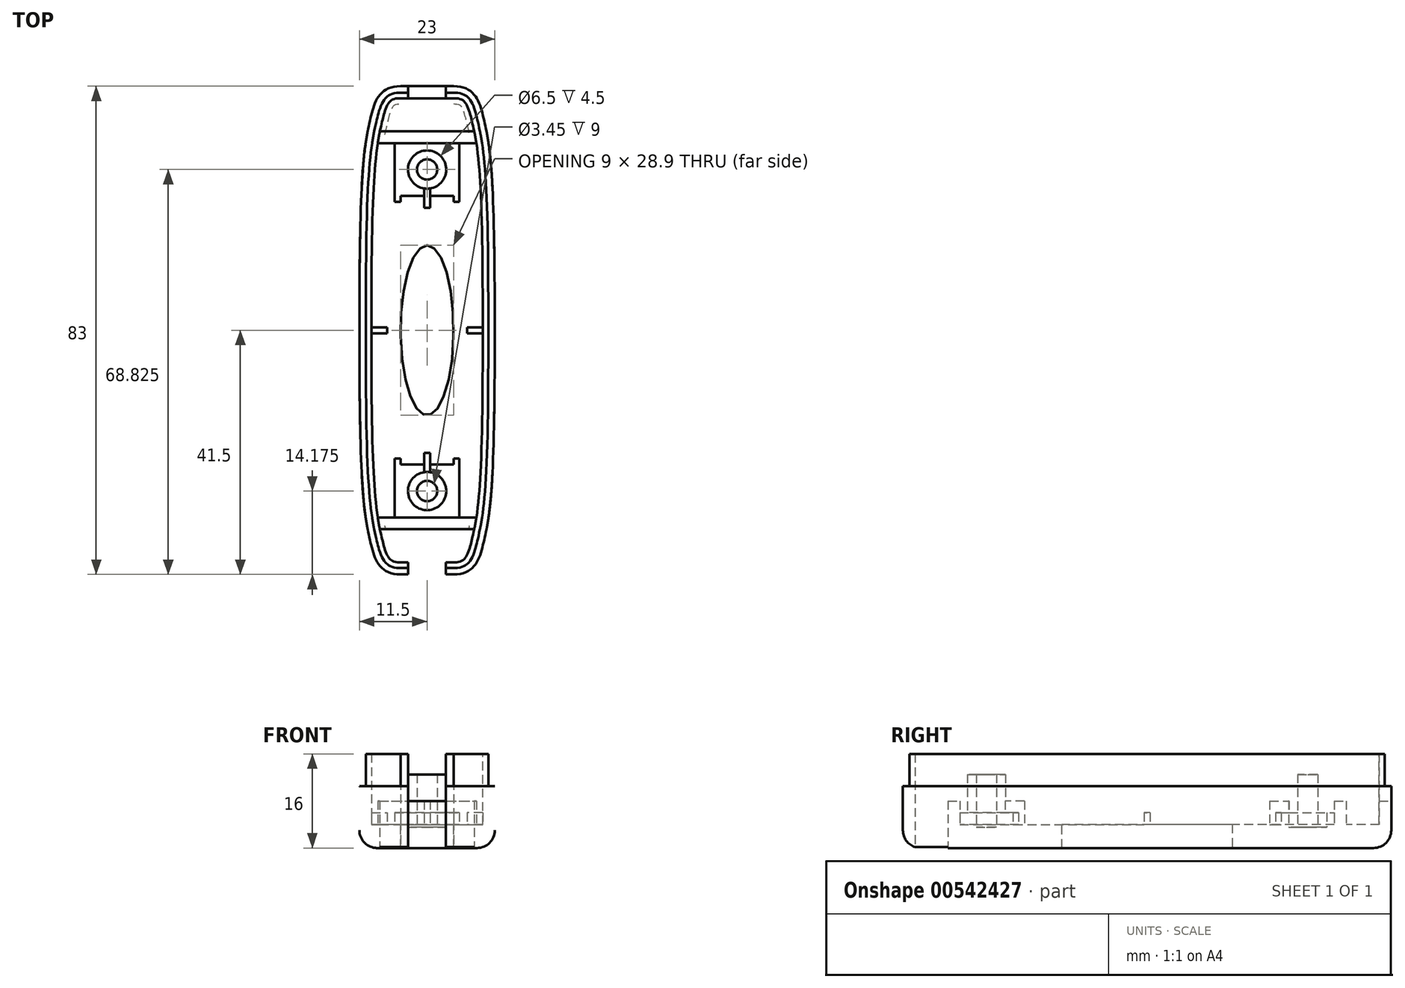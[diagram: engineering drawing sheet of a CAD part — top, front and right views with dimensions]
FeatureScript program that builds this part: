
annotation { "Feature Type Name" : "Feature", "Feature Type Description" : "" }
export const myFeature = defineFeature(function(context is Context, id is Id, definition is map)
    precondition{}
    {
        {
            var Q0;
            Q0=qCreatedBy(makeId("Top.planeOp"),FACE);
            var sketch = newSketch(context, id + "F0", { "sketchPlane" : qUnion([Q0])});
            skLineSegment(sketch, "E0.bottom", {"start": v(4.5, 14.45) * mm, "end": v(-4.5, 14.45) * mm, "construction": true});
            skLineSegment(sketch, "E0.top", {"start": v(4.5, -14.45) * mm, "end": v(-4.5, -14.45) * mm, "construction": true});
            skLineSegment(sketch, "E0.left", {"start": v(4.5, 14.45) * mm, "end": v(4.5, -14.45) * mm, "construction": true});
            skLineSegment(sketch, "E0.right", {"start": v(-4.5, 14.45) * mm, "end": v(-4.5, -14.45) * mm, "construction": true});
            skPoint(sketch, "E0.middle", {"position": v(0, 0) * mm});
            skPoint(sketch, "E1", {"position": v(0, 14.45) * mm});
            skPoint(sketch, "E2", {"position": v(4.5, 0) * mm});
            skEllipse(sketch, "E3", {"center": v(0, 0) * mm, "majorRadius": 14.45 * mm, "minorRadius": 4.5 * mm, "majorAxis": v(0, 1)});
            skLineSegment(sketch, "E4.bottom", {"start": v(11.5, 41.5) * mm, "end": v(-11.5, 41.5) * mm, "construction": true});
            skLineSegment(sketch, "E4.top", {"start": v(11.5, -41.5) * mm, "end": v(-11.5, -41.5) * mm, "construction": true});
            skLineSegment(sketch, "E4.left", {"start": v(11.5, 41.5) * mm, "end": v(11.5, -41.5) * mm, "construction": true});
            skLineSegment(sketch, "E4.right", {"start": v(-11.5, 41.5) * mm, "end": v(-11.5, -41.5) * mm, "construction": true});
            skLineSegment(sketch, "E5", {"start": v(11.5, 0) * mm, "end": v(-11.5, 0) * mm, "construction": true});
            skLineSegment(sketch, "E6.bottom", {"start": v(-11.5, 0.5) * mm, "end": v(-6.8, 0.5) * mm});
            skLineSegment(sketch, "E6.top", {"start": v(-11.5, -0.5) * mm, "end": v(-6.8, -0.5) * mm});
            skLineSegment(sketch, "E6.left", {"start": v(-11.5, 0.5) * mm, "end": v(-11.5, -0.5) * mm});
            skLineSegment(sketch, "E6.right", {"start": v(-6.8, 0.5) * mm, "end": v(-6.8, -0.5) * mm});
            skLineSegment(sketch, "E7.MirrorCS", {"start": v(6.8, 0.5) * mm, "end": v(6.8, -0.5) * mm});
            skLineSegment(sketch, "E8.MirrorCS", {"start": v(11.5, 0.5) * mm, "end": v(11.5, -0.5) * mm});
            skLineSegment(sketch, "E9.MirrorCS", {"start": v(11.5, -0.5) * mm, "end": v(6.8, -0.5) * mm});
            skLineSegment(sketch, "E10.MirrorCS", {"start": v(11.5, 0.5) * mm, "end": v(6.8, 0.5) * mm});
            skLineSegment(sketch, "E11.bottom", {"start": v(-9.5, 41.5) * mm, "end": v(9.5, 41.5) * mm, "construction": true});
            skLineSegment(sketch, "E11.top", {"start": v(-9.5, -41.5) * mm, "end": v(9.5, -41.5) * mm, "construction": true});
            skLineSegment(sketch, "E11.left", {"start": v(-9.5, 41.5) * mm, "end": v(-9.5, -41.5) * mm, "construction": true});
            skLineSegment(sketch, "E11.right", {"start": v(9.5, 41.5) * mm, "end": v(9.5, -41.5) * mm, "construction": true});
            skLineSegment(sketch, "E12", {"start": v(-9.5, -36.5) * mm, "end": v(9.5, -36.5) * mm, "construction": true});
            skLineSegment(sketch, "E13.MirrorCS", {"start": v(-9.5, 36.5) * mm, "end": v(9.5, 36.5) * mm, "construction": true});
            skLineSegment(sketch, "E14.bottom", {"start": v(-4.5, 41.5) * mm, "end": v(4.5, 41.5) * mm, "construction": true});
            skLineSegment(sketch, "E14.top", {"start": v(-4.5, -41.5) * mm, "end": v(4.5, -41.5) * mm, "construction": true});
            skLineSegment(sketch, "E14.left", {"start": v(-4.5, 41.5) * mm, "end": v(-4.5, -41.5) * mm, "construction": true});
            skLineSegment(sketch, "E14.right", {"start": v(4.5, 41.5) * mm, "end": v(4.5, -41.5) * mm, "construction": true});
            skLineSegment(sketch, "E15", {"start": v(-4.5, -41.5) * mm, "end": v(4.5, -41.5) * mm});
            skFitSpline(sketch, "E16", {"points": [v(4.5, -41.5) * mm, v(9.5, -36.5) * mm, v(11.5, 0) * mm], "startDerivative": vector(35.32, 0) * mm, "endDerivative": vector(0, 110.7) * mm});
            skFitSpline(sketch, "E17.MirrorCS", {"points": [v(-4.5, -41.5) * mm, v(-9.5, -36.5) * mm, v(-11.5, 0) * mm], "startDerivative": vector(-35.32, 0) * mm, "endDerivative": vector(0, 110.7) * mm});
            skFitSpline(sketch, "E18.MirrorCS", {"points": [v(4.5, 41.5) * mm, v(9.5, 36.5) * mm, v(11.5, 0) * mm], "startDerivative": vector(35.32, 0) * mm, "endDerivative": vector(0, -110.7) * mm});
            skFitSpline(sketch, "E19.MirrorCS", {"points": [v(-4.5, 41.5) * mm, v(-9.5, 36.5) * mm, v(-11.5, 0) * mm], "startDerivative": vector(-35.32, 0) * mm, "endDerivative": vector(0, -110.7) * mm});
            skLineSegment(sketch, "E20.MirrorCS", {"start": v(-4.5, 41.5) * mm, "end": v(4.5, 41.5) * mm});
            skLineSegment(sketch, "E21.bottom", {"start": v(5.5, 22.82) * mm, "end": v(-5.5, 22.82) * mm, "construction": true});
            skLineSegment(sketch, "E21.top", {"start": v(5.5, -22.82) * mm, "end": v(-5.5, -22.82) * mm, "construction": true});
            skLineSegment(sketch, "E21.left", {"start": v(5.5, 22.82) * mm, "end": v(5.5, -22.82) * mm, "construction": true});
            skLineSegment(sketch, "E21.right", {"start": v(-5.5, 22.82) * mm, "end": v(-5.5, -22.82) * mm, "construction": true});
            skLineSegment(sketch, "E22", {"start": v(-0.5, -22.82) * mm, "end": v(-0.5, -20.82) * mm});
            skLineSegment(sketch, "E23", {"start": v(-0.5, -20.82) * mm, "end": v(0.5, -20.82) * mm});
            skLineSegment(sketch, "E24", {"start": v(0.5, -20.82) * mm, "end": v(0.5, -22.82) * mm});
            skLineSegment(sketch, "E25", {"start": v(-0.5, -22.82) * mm, "end": v(-4.5, -22.82) * mm});
            skLineSegment(sketch, "E26", {"start": v(-4.5, -22.82) * mm, "end": v(-4.5, -21.82) * mm});
            skLineSegment(sketch, "E27", {"start": v(-4.5, -21.82) * mm, "end": v(-5.5, -21.82) * mm});
            skLineSegment(sketch, "E28", {"start": v(-5.5, -21.82) * mm, "end": v(-5.5, -31.82) * mm});
            skLineSegment(sketch, "E29", {"start": v(-5.5, -31.82) * mm, "end": v(5.5, -31.82) * mm});
            skLineSegment(sketch, "E30", {"start": v(5.5, -31.82) * mm, "end": v(5.5, -22.82) * mm});
            skLineSegment(sketch, "E31", {"start": v(5.5, -21.82) * mm, "end": v(4.5, -21.82) * mm});
            skLineSegment(sketch, "E32", {"start": v(4.5, -21.82) * mm, "end": v(4.5, -22.82) * mm});
            skLineSegment(sketch, "E33", {"start": v(4.5, -22.82) * mm, "end": v(0.5, -22.82) * mm});
            skLineSegment(sketch, "E34", {"start": v(5.5, -21.82) * mm, "end": v(5.5, -22.82) * mm});
            skLineSegment(sketch, "E35.MirrorCS", {"start": v(-0.5, 22.82) * mm, "end": v(-4.5, 22.82) * mm});
            skLineSegment(sketch, "E36.MirrorCS", {"start": v(-4.5, 22.82) * mm, "end": v(-4.5, 21.82) * mm});
            skLineSegment(sketch, "E37.MirrorCS", {"start": v(-4.5, 21.82) * mm, "end": v(-5.5, 21.82) * mm});
            skLineSegment(sketch, "E38.MirrorCS", {"start": v(-5.5, 21.82) * mm, "end": v(-5.5, 31.82) * mm});
            skLineSegment(sketch, "E39.MirrorCS", {"start": v(-5.5, 31.82) * mm, "end": v(5.5, 31.82) * mm});
            skLineSegment(sketch, "E40.MirrorCS", {"start": v(5.5, 31.82) * mm, "end": v(5.5, 22.82) * mm});
            skLineSegment(sketch, "E41.MirrorCS", {"start": v(5.5, 21.82) * mm, "end": v(5.5, 22.82) * mm});
            skLineSegment(sketch, "E42.MirrorCS", {"start": v(5.5, 21.82) * mm, "end": v(4.5, 21.82) * mm});
            skLineSegment(sketch, "E43.MirrorCS", {"start": v(4.5, 21.82) * mm, "end": v(4.5, 22.82) * mm});
            skLineSegment(sketch, "E44.MirrorCS", {"start": v(4.5, 22.82) * mm, "end": v(0.5, 22.82) * mm});
            skLineSegment(sketch, "E45.MirrorCS", {"start": v(0.5, 20.82) * mm, "end": v(0.5, 22.82) * mm});
            skLineSegment(sketch, "E46.MirrorCS", {"start": v(-0.5, 20.82) * mm, "end": v(0.5, 20.82) * mm});
            skLineSegment(sketch, "E47.MirrorCS", {"start": v(-0.5, 22.82) * mm, "end": v(-0.5, 20.82) * mm});
            skLineSegment(sketch, "E48", {"start": v(-5.5, -31.82) * mm, "end": v(-10.44, -31.82) * mm});
            skLineSegment(sketch, "E49", {"start": v(5.5, -31.82) * mm, "end": v(10.44, -31.82) * mm});
            skLineSegment(sketch, "E50", {"start": v(-10.1, -33.83) * mm, "end": v(10.1, -33.83) * mm});
            skLineSegment(sketch, "E51.MirrorCS", {"start": v(-5.5, 31.82) * mm, "end": v(-10.44, 31.82) * mm});
            skLineSegment(sketch, "E52.MirrorCS", {"start": v(-10.1, 33.83) * mm, "end": v(10.1, 33.83) * mm});
            skLineSegment(sketch, "E53.MirrorCS", {"start": v(5.5, 31.82) * mm, "end": v(10.44, 31.82) * mm});
            skLineSegment(sketch, "E54", {"start": v(-4.5, -22.82) * mm, "end": v(4.5, -31.82) * mm, "construction": true});
            skLineSegment(sketch, "E55", {"start": v(4.5, -22.82) * mm, "end": v(-4.5, -31.82) * mm, "construction": true});
            skPoint(sketch, "E56", {"position": v(0, -27.32) * mm});
            skCircle(sketch, "E57", {"center": v(0, -27.32) * mm, "radius": 3.25 * mm});
            skCircle(sketch, "E58", {"center": v(0, -27.32) * mm, "radius": 1.73 * mm});
            skCircle(sketch, "E59.MirrorC", {"center": v(0, 27.32) * mm, "radius": 1.73 * mm});
            skCircle(sketch, "E60.MirrorC", {"center": v(0, 27.32) * mm, "radius": 3.25 * mm});
            skLineSegment(sketch, "E61", {"start": v(-0.5, -22.82) * mm, "end": v(-0.5, -24.11) * mm});
            skLineSegment(sketch, "E62", {"start": v(0.5, -22.82) * mm, "end": v(0.5, -24.11) * mm});
            skLineSegment(sketch, "E63", {"start": v(-0.5, -22.82) * mm, "end": v(0.5, -22.82) * mm});
            skLineSegment(sketch, "E64.MirrorCS", {"start": v(-0.5, 22.82) * mm, "end": v(-0.5, 24.11) * mm});
            skLineSegment(sketch, "E65.MirrorCS", {"start": v(0.5, 22.82) * mm, "end": v(0.5, 24.11) * mm});
            skLineSegment(sketch, "E66.MirrorCS", {"start": v(-0.5, 22.82) * mm, "end": v(0.5, 22.82) * mm});
            skLineSegment(sketch, "E67.0", {"start": v(-4.5, 39.45) * mm, "end": v(4.5, 39.45) * mm});
            skFitSpline(sketch, "E67.1", {"points": [v(4.5, -39.45) * mm, v(4.77, -39.45) * mm, v(5.23, -39.41) * mm, v(5.7, -39.28) * mm, v(6.03, -39.12) * mm, v(6.28, -38.93) * mm, v(6.52, -38.66) * mm, v(6.75, -38.29) * mm, v(6.97, -37.8) * mm, v(7.18, -37.22) * mm, v(7.34, -36.67) * mm, v(7.46, -36.2) * mm, v(7.59, -35.71) * mm, v(7.73, -35.1) * mm, v(7.95, -34.13) * mm, v(8.2, -32.87) * mm, v(8.47, -31.18) * mm, v(8.7, -29.22) * mm, v(8.91, -26.9) * mm, v(9.08, -24.1) * mm, v(9.26, -19.65) * mm, v(9.41, -12.5) * mm, v(9.45, -4.6) * mm, v(9.45, 0) * mm]});
            skLineSegment(sketch, "E67.2", {"start": v(-4.5, -39.45) * mm, "end": v(4.5, -39.45) * mm});
            skFitSpline(sketch, "E67.3", {"points": [v(4.5, 39.45) * mm, v(4.77, 39.45) * mm, v(5.23, 39.41) * mm, v(5.7, 39.28) * mm, v(6.03, 39.12) * mm, v(6.28, 38.93) * mm, v(6.52, 38.66) * mm, v(6.75, 38.29) * mm, v(6.97, 37.8) * mm, v(7.18, 37.22) * mm, v(7.34, 36.67) * mm, v(7.46, 36.2) * mm, v(7.59, 35.71) * mm, v(7.73, 35.1) * mm, v(7.95, 34.13) * mm, v(8.2, 32.87) * mm, v(8.47, 31.18) * mm, v(8.7, 29.22) * mm, v(8.91, 26.9) * mm, v(9.08, 24.1) * mm, v(9.26, 19.65) * mm, v(9.41, 12.5) * mm, v(9.45, 4.6) * mm, v(9.45, 0) * mm]});
            skFitSpline(sketch, "E67.4", {"points": [v(-4.5, -39.45) * mm, v(-4.77, -39.45) * mm, v(-5.23, -39.41) * mm, v(-5.7, -39.28) * mm, v(-6.03, -39.12) * mm, v(-6.28, -38.93) * mm, v(-6.52, -38.66) * mm, v(-6.75, -38.29) * mm, v(-6.97, -37.8) * mm, v(-7.18, -37.22) * mm, v(-7.34, -36.67) * mm, v(-7.46, -36.2) * mm, v(-7.59, -35.71) * mm, v(-7.73, -35.1) * mm, v(-7.95, -34.13) * mm, v(-8.2, -32.87) * mm, v(-8.47, -31.18) * mm, v(-8.7, -29.22) * mm, v(-8.91, -26.9) * mm, v(-9.08, -24.1) * mm, v(-9.26, -19.65) * mm, v(-9.41, -12.5) * mm, v(-9.45, -4.6) * mm, v(-9.45, 0) * mm]});
            skFitSpline(sketch, "E67.5", {"points": [v(-4.5, 39.45) * mm, v(-4.77, 39.45) * mm, v(-5.23, 39.41) * mm, v(-5.7, 39.28) * mm, v(-6.03, 39.12) * mm, v(-6.28, 38.93) * mm, v(-6.52, 38.66) * mm, v(-6.75, 38.29) * mm, v(-6.97, 37.8) * mm, v(-7.18, 37.22) * mm, v(-7.34, 36.67) * mm, v(-7.46, 36.2) * mm, v(-7.59, 35.71) * mm, v(-7.73, 35.1) * mm, v(-7.95, 34.13) * mm, v(-8.2, 32.87) * mm, v(-8.47, 31.18) * mm, v(-8.7, 29.22) * mm, v(-8.91, 26.9) * mm, v(-9.08, 24.1) * mm, v(-9.26, 19.65) * mm, v(-9.41, 12.5) * mm, v(-9.45, 4.6) * mm, v(-9.45, 0) * mm]});
            skLineSegment(sketch, "E68.0", {"start": v(-4.5, -40.4) * mm, "end": v(4.5, -40.4) * mm});
            skFitSpline(sketch, "E68.1", {"points": [v(-4.5, 40.4) * mm, v(-4.82, 40.4) * mm, v(-5.37, 40.35) * mm, v(-5.92, 40.21) * mm, v(-6.28, 40.06) * mm, v(-6.52, 39.93) * mm, v(-6.73, 39.78) * mm, v(-6.93, 39.6) * mm, v(-7.11, 39.42) * mm, v(-7.34, 39.14) * mm, v(-7.6, 38.73) * mm, v(-7.86, 38.16) * mm, v(-8.09, 37.5) * mm, v(-8.25, 36.92) * mm, v(-8.38, 36.44) * mm, v(-8.5, 35.94) * mm, v(-8.66, 35.32) * mm, v(-8.88, 34.33) * mm, v(-9.14, 33.03) * mm, v(-9.41, 31.3) * mm, v(-9.65, 29.31) * mm, v(-9.93, 26.17) * mm, v(-10.18, 21.11) * mm, v(-10.36, 12.5) * mm, v(-10.4, 4.6) * mm, v(-10.4, 0) * mm]});
            skLineSegment(sketch, "E68.2", {"start": v(-4.5, 40.4) * mm, "end": v(4.5, 40.4) * mm});
            skFitSpline(sketch, "E68.3", {"points": [v(-4.5, -40.4) * mm, v(-4.82, -40.4) * mm, v(-5.37, -40.35) * mm, v(-5.92, -40.21) * mm, v(-6.28, -40.06) * mm, v(-6.52, -39.93) * mm, v(-6.73, -39.78) * mm, v(-6.93, -39.6) * mm, v(-7.11, -39.42) * mm, v(-7.34, -39.14) * mm, v(-7.6, -38.73) * mm, v(-7.86, -38.16) * mm, v(-8.09, -37.5) * mm, v(-8.25, -36.92) * mm, v(-8.38, -36.44) * mm, v(-8.5, -35.94) * mm, v(-8.66, -35.32) * mm, v(-8.88, -34.33) * mm, v(-9.14, -33.03) * mm, v(-9.41, -31.3) * mm, v(-9.65, -29.31) * mm, v(-9.93, -26.17) * mm, v(-10.18, -21.11) * mm, v(-10.36, -12.5) * mm, v(-10.4, -4.6) * mm, v(-10.4, 0) * mm]});
            skFitSpline(sketch, "E68.4", {"points": [v(4.5, 40.4) * mm, v(4.82, 40.4) * mm, v(5.37, 40.35) * mm, v(5.92, 40.21) * mm, v(6.28, 40.06) * mm, v(6.52, 39.93) * mm, v(6.73, 39.78) * mm, v(6.93, 39.6) * mm, v(7.11, 39.42) * mm, v(7.34, 39.14) * mm, v(7.6, 38.73) * mm, v(7.86, 38.16) * mm, v(8.09, 37.5) * mm, v(8.25, 36.92) * mm, v(8.38, 36.44) * mm, v(8.5, 35.94) * mm, v(8.66, 35.32) * mm, v(8.88, 34.33) * mm, v(9.14, 33.03) * mm, v(9.41, 31.3) * mm, v(9.65, 29.31) * mm, v(9.93, 26.17) * mm, v(10.18, 21.11) * mm, v(10.36, 12.5) * mm, v(10.4, 4.6) * mm, v(10.4, 0) * mm]});
            skFitSpline(sketch, "E68.5", {"points": [v(4.5, -40.4) * mm, v(4.82, -40.4) * mm, v(5.37, -40.35) * mm, v(5.92, -40.21) * mm, v(6.28, -40.06) * mm, v(6.52, -39.93) * mm, v(6.73, -39.78) * mm, v(6.93, -39.6) * mm, v(7.11, -39.42) * mm, v(7.34, -39.14) * mm, v(7.6, -38.73) * mm, v(7.86, -38.16) * mm, v(8.09, -37.5) * mm, v(8.25, -36.92) * mm, v(8.38, -36.44) * mm, v(8.5, -35.94) * mm, v(8.66, -35.32) * mm, v(8.88, -34.33) * mm, v(9.14, -33.03) * mm, v(9.41, -31.3) * mm, v(9.65, -29.31) * mm, v(9.93, -26.17) * mm, v(10.18, -21.11) * mm, v(10.36, -12.5) * mm, v(10.4, -4.6) * mm, v(10.4, 0) * mm]});
            skLineSegment(sketch, "E69.bottom", {"start": v(-3.2, -39.45) * mm, "end": v(3.2, -39.45) * mm});
            skLineSegment(sketch, "E69.top", {"start": v(-3.2, -41.5) * mm, "end": v(3.2, -41.5) * mm});
            skLineSegment(sketch, "E69.left", {"start": v(-3.2, -39.45) * mm, "end": v(-3.2, -41.5) * mm});
            skLineSegment(sketch, "E69.right", {"start": v(3.2, -39.45) * mm, "end": v(3.2, -41.5) * mm});
            skLineSegment(sketch, "E70.MirrorCS", {"start": v(-3.2, 39.45) * mm, "end": v(-3.2, 41.5) * mm});
            skLineSegment(sketch, "E71.MirrorCS", {"start": v(3.2, 39.45) * mm, "end": v(3.2, 41.5) * mm});
            skLineSegment(sketch, "E72", {"start": v(-3.2, -33.83) * mm, "end": v(-3.2, -31.82) * mm});
            skLineSegment(sketch, "E73", {"start": v(3.2, -33.83) * mm, "end": v(3.2, -31.82) * mm});
            skLineSegment(sketch, "E74.MirrorCS", {"start": v(-3.2, 33.83) * mm, "end": v(-3.2, 31.82) * mm});
            skLineSegment(sketch, "E75.MirrorCS", {"start": v(3.2, 33.83) * mm, "end": v(3.2, 31.82) * mm});
            skFitSpline(sketch, "E76.0", {"points": [v(0.78, 17.9) * mm, v(0, 17.97) * mm, v(-0.78, 17.9) * mm, v(-1.76, 17.67) * mm, v(-2.81, 17.15) * mm, v(-3.78, 16.35) * mm, v(-4.54, 15.47) * mm, v(-5.16, 14.52) * mm, v(-5.86, 13.16) * mm, v(-6.56, 11.3) * mm, v(-7.1, 9.21) * mm, v(-7.43, 7.4) * mm, v(-7.7, 5.5) * mm, v(-7.9, 3.55) * mm, v(-7.98, 1.53) * mm, v(-8, 0) * mm, v(-7.98, -1.53) * mm, v(-7.9, -3.55) * mm, v(-7.7, -5.5) * mm, v(-7.43, -7.4) * mm, v(-7.1, -9.21) * mm, v(-6.56, -11.3) * mm, v(-5.86, -13.16) * mm, v(-5.16, -14.52) * mm, v(-4.54, -15.47) * mm, v(-3.78, -16.35) * mm, v(-2.81, -17.15) * mm, v(-1.76, -17.67) * mm, v(-0.78, -17.9) * mm, v(0, -17.97) * mm, v(0.78, -17.9) * mm, v(1.76, -17.67) * mm, v(2.81, -17.15) * mm, v(3.78, -16.35) * mm, v(4.54, -15.47) * mm, v(5.16, -14.52) * mm, v(5.86, -13.16) * mm, v(6.56, -11.3) * mm, v(7.1, -9.21) * mm, v(7.43, -7.4) * mm, v(7.7, -5.5) * mm, v(7.9, -3.55) * mm, v(7.98, -1.53) * mm, v(8, 0) * mm, v(7.98, 1.53) * mm, v(7.9, 3.55) * mm, v(7.7, 5.5) * mm, v(7.43, 7.4) * mm, v(7.1, 9.21) * mm, v(6.56, 11.3) * mm, v(5.86, 13.16) * mm, v(5.16, 14.52) * mm, v(4.54, 15.47) * mm, v(3.78, 16.35) * mm, v(2.81, 17.15) * mm, v(1.76, 17.67) * mm, v(0.78, 17.9) * mm, v(0, 17.97) * mm, v(-0.78, 17.9) * mm, v(0.78, 17.9) * mm]});
            skSolve(sketch);
        }
        {
            var Q0;
            Q0=makeQuery(id+"F0.imprint","IMPRINT",FACE,{"disambiguationData":[TD([[makeQuery(id+"F0.imprint","IMPRINT",EDGE,{"derivedFrom":sQuery(id+"F0.wireOp",EDGE,"E3")}),-1.0]])]});
            extrude(context, id + "F1", {"entities" : qUnion([Q0]), "depth" : 2.2 * mm, "offsetDistance" : 25 * mm});
        }
        {
            var Q0;
            Q0=makeQuery(id+"F0.imprint","IMPRINT",FACE,{"disambiguationData":[TD([[makeQuery(id+"F0.imprint","IMPRINT",EDGE,{"derivedFrom":sQuery(id+"F0.wireOp",EDGE,"E36.MirrorCS")}),1.0]])]});
            var Q1;
            Q1=makeQuery(id+"F0.imprint","IMPRINT",FACE,{"disambiguationData":[TD([[makeQuery(id+"F0.imprint","IMPRINT",EDGE,{"derivedFrom":sQuery(id+"F0.wireOp",EDGE,"E22")}),1.0]])]});
            var Q2;
            {var subQ10=sQuery(id+"F0.wireOp",EDGE,"E69.bottom");Q2=makeQuery(id+"F0.imprint","IMPRINT",FACE,{"disambiguationData":[TD([[makeQuery(id+"F0.imprint","IMPRINT",EDGE,{"derivedFrom":subQ10}),1.0]])]});}
            var Q3;
            {var subQ0=sQuery(id+"F0.wireOp",EDGE,"E52.MirrorCS");var subQ4=makeQuery(id+"F0.imprint","INTERSECT",VERTEX,{"derivedFrom":[subQ0,sQuery(id+"F0.wireOp",EDGE,"E74.MirrorCS")]});Q3=makeQuery(id+"F0.imprint","IMPRINT",FACE,{"disambiguationData":[TD([[makeQuery(id+"F0.imprint","IMPRINT",EDGE,{"disambiguationData":[TD([[subQ4,1.0]])],"derivedFrom":subQ0}),1.0]])]});}
            extrude(context, id + "F2", {"entities" : qUnion([Q0, Q1, Q2, Q3]), "operationType" : NewBodyOperationType.ADD, "depth" : 4 * mm, "offsetDistance" : 25 * mm});
        }
        {
            var Q0;
            {var subQ5=sQuery(id+"F0.wireOp",EDGE,"E6.right");Q0=makeQuery(id+"F0.imprint","IMPRINT",FACE,{"disambiguationData":[TD([[makeQuery(id+"F0.imprint","IMPRINT",EDGE,{"derivedFrom":subQ5}),-1.0]])]});}
            var Q1;
            {var subQ6=sQuery(id+"F0.wireOp",EDGE,"E7.MirrorCS");Q1=makeQuery(id+"F0.imprint","IMPRINT",FACE,{"disambiguationData":[TD([[makeQuery(id+"F0.imprint","IMPRINT",EDGE,{"derivedFrom":subQ6}),1.0]])]});}
            var Q2;
            Q2=makeQuery(id+"F0.imprint","IMPRINT",FACE,{"disambiguationData":[TD([[makeQuery(id+"F0.imprint","IMPRINT",EDGE,{"derivedFrom":sQuery(id+"F0.wireOp",EDGE,"E36.MirrorCS")}),-1.0]])]});
            var Q3;
            Q3=makeQuery(id+"F0.imprint","IMPRINT",FACE,{"disambiguationData":[TD([[makeQuery(id+"F0.imprint","IMPRINT",EDGE,{"derivedFrom":sQuery(id+"F0.wireOp",EDGE,"E25")}),1.0]])]});
            var Q4;
            {var subQ0=sQuery(id+"F0.wireOp",EDGE,"E67.5");var subQ5=sQuery(id+"F0.wireOp",EDGE,"E6.bottom");var subQ6=makeQuery(id+"F0.imprint","INTERSECT",VERTEX,{"derivedFrom":[subQ5,subQ0]});Q4=makeQuery(id+"F0.imprint","IMPRINT",FACE,{"disambiguationData":[TD([[makeQuery(id+"F0.imprint","IMPRINT",EDGE,{"disambiguationData":[TD([[subQ6,-1.0]])],"derivedFrom":subQ5}),-1.0]])]});}
            var Q5;
            {var subQ1=sQuery(id+"F0.wireOp",EDGE,"E67.1");var subQ5=sQuery(id+"F0.wireOp",EDGE,"E9.MirrorCS");var subQ6=makeQuery(id+"F0.imprint","INTERSECT",VERTEX,{"derivedFrom":[subQ5,subQ1]});Q5=makeQuery(id+"F0.imprint","IMPRINT",FACE,{"disambiguationData":[TD([[makeQuery(id+"F0.imprint","IMPRINT",EDGE,{"disambiguationData":[TD([[subQ6,-1.0]])],"derivedFrom":subQ5}),-1.0]])]});}
            extrude(context, id + "F3", {"entities" : qUnion([Q0, Q1, Q2, Q3, Q4, Q5]), "operationType" : NewBodyOperationType.ADD, "depth" : 6 * mm, "offsetDistance" : 25 * mm});
        }
        {
            var Q0;
            Q0=makeQuery(id+"F0.imprint","IMPRINT",FACE,{"disambiguationData":[TD([[makeQuery(id+"F0.imprint","IMPRINT",EDGE,{"derivedFrom":sQuery(id+"F0.wireOp",EDGE,"E22")}),-1.0]])]});
            var Q1;
            {var subQ0=sQuery(id+"F0.wireOp",EDGE,"E61");Q1=makeQuery(id+"F0.imprint","IMPRINT",FACE,{"disambiguationData":[TD([[makeQuery(id+"F0.imprint","IMPRINT",EDGE,{"derivedFrom":subQ0}),1.0]])]});}
            var Q2;
            {var subQ0=sQuery(id+"F0.wireOp",EDGE,"E64.MirrorCS");Q2=makeQuery(id+"F0.imprint","IMPRINT",FACE,{"disambiguationData":[TD([[makeQuery(id+"F0.imprint","IMPRINT",EDGE,{"derivedFrom":subQ0}),-1.0]])]});}
            var Q3;
            Q3=makeQuery(id+"F0.imprint","IMPRINT",FACE,{"disambiguationData":[TD([[makeQuery(id+"F0.imprint","IMPRINT",EDGE,{"derivedFrom":sQuery(id+"F0.wireOp",EDGE,"E45.MirrorCS")}),1.0]])]});
            extrude(context, id + "F4", {"entities" : qUnion([Q0, Q1, Q2, Q3]), "operationType" : NewBodyOperationType.ADD, "depth" : 8 * mm, "offsetDistance" : 25 * mm});
        }
        {
            var Q0;
            {var subQ0=sQuery(id+"F0.wireOp",EDGE,"E18.MirrorCS");var subQ1=sQuery(id+"F0.wireOp",EDGE,"E10.MirrorCS");var subQ2=makeQuery(id+"F0.imprint","INTERSECT",VERTEX,{"derivedFrom":[subQ1,subQ0]});Q0=makeQuery(id+"F0.imprint","IMPRINT",FACE,{"disambiguationData":[TD([[makeQuery(id+"F0.imprint","IMPRINT",EDGE,{"disambiguationData":[TD([[subQ2,-1.0]])],"derivedFrom":subQ1}),-1.0]])]});}
            var Q1;
            {var subQ3=sQuery(id+"F0.wireOp",EDGE,"E16");var subQ8=sQuery(id+"F0.wireOp",EDGE,"E9.MirrorCS");var subQ10=makeQuery(id+"F0.imprint","INTERSECT",VERTEX,{"derivedFrom":[subQ8,subQ3]});Q1=makeQuery(id+"F0.imprint","IMPRINT",FACE,{"disambiguationData":[TD([[makeQuery(id+"F0.imprint","IMPRINT",EDGE,{"disambiguationData":[TD([[subQ10,-1.0]])],"derivedFrom":subQ8}),-1.0]])]});}
            var Q2;
            {var subQ0=sQuery(id+"F0.wireOp",EDGE,"E16");var subQ1=sQuery(id+"F0.wireOp",EDGE,"E9.MirrorCS");var subQ2=makeQuery(id+"F0.imprint","INTERSECT",VERTEX,{"derivedFrom":[subQ1,subQ0]});Q2=makeQuery(id+"F0.imprint","IMPRINT",FACE,{"disambiguationData":[TD([[makeQuery(id+"F0.imprint","IMPRINT",EDGE,{"disambiguationData":[TD([[subQ2,-1.0]])],"derivedFrom":subQ1}),1.0]])]});}
            var Q3;
            {var subQ0=sQuery(id+"F0.wireOp",EDGE,"E49");var subQ1=sQuery(id+"F0.wireOp",EDGE,"E16");var subQ2=makeQuery(id+"F0.imprint","INTERSECT",VERTEX,{"derivedFrom":[subQ1,subQ0]});Q3=makeQuery(id+"F0.imprint","IMPRINT",FACE,{"disambiguationData":[TD([[makeQuery(id+"F0.imprint","IMPRINT",EDGE,{"disambiguationData":[TD([[subQ2,1.0]])],"derivedFrom":subQ1}),1.0]])]});}
            var Q4;
            {var subQ6=sQuery(id+"F0.wireOp",EDGE,"E16");var subQ9=sQuery(id+"F0.wireOp",EDGE,"E15");var subQ10=makeQuery(id+"F0.imprint","INTERSECT",VERTEX,{"derivedFrom":[subQ9,subQ6]});Q4=makeQuery(id+"F0.imprint","IMPRINT",FACE,{"disambiguationData":[TD([[makeQuery(id+"F0.imprint","IMPRINT",EDGE,{"disambiguationData":[TD([[subQ10,-1.0]])],"derivedFrom":subQ6}),1.0]])]});}
            var Q5;
            {var subQ6=sQuery(id+"F0.wireOp",EDGE,"E17.MirrorCS");var subQ9=sQuery(id+"F0.wireOp",EDGE,"E15");var subQ10=makeQuery(id+"F0.imprint","INTERSECT",VERTEX,{"derivedFrom":[subQ9,subQ6]});Q5=makeQuery(id+"F0.imprint","IMPRINT",FACE,{"disambiguationData":[TD([[makeQuery(id+"F0.imprint","IMPRINT",EDGE,{"disambiguationData":[TD([[subQ10,-1.0]])],"derivedFrom":subQ6}),-1.0]])]});}
            var Q6;
            {var subQ0=sQuery(id+"F0.wireOp",EDGE,"E48");var subQ1=sQuery(id+"F0.wireOp",EDGE,"E17.MirrorCS");var subQ2=makeQuery(id+"F0.imprint","INTERSECT",VERTEX,{"derivedFrom":[subQ1,subQ0]});Q6=makeQuery(id+"F0.imprint","IMPRINT",FACE,{"disambiguationData":[TD([[makeQuery(id+"F0.imprint","IMPRINT",EDGE,{"disambiguationData":[TD([[subQ2,1.0]])],"derivedFrom":subQ1}),-1.0]])]});}
            var Q7;
            {var subQ0=sQuery(id+"F0.wireOp",EDGE,"E17.MirrorCS");var subQ1=sQuery(id+"F0.wireOp",EDGE,"E6.top");var subQ2=makeQuery(id+"F0.imprint","INTERSECT",VERTEX,{"derivedFrom":[subQ1,subQ0]});Q7=makeQuery(id+"F0.imprint","IMPRINT",FACE,{"disambiguationData":[TD([[makeQuery(id+"F0.imprint","IMPRINT",EDGE,{"disambiguationData":[TD([[subQ2,-1.0]])],"derivedFrom":subQ1}),-1.0]])]});}
            var Q8;
            {var subQ0=sQuery(id+"F0.wireOp",EDGE,"E19.MirrorCS");var subQ1=sQuery(id+"F0.wireOp",EDGE,"E6.bottom");var subQ2=makeQuery(id+"F0.imprint","INTERSECT",VERTEX,{"derivedFrom":[subQ1,subQ0]});Q8=makeQuery(id+"F0.imprint","IMPRINT",FACE,{"disambiguationData":[TD([[makeQuery(id+"F0.imprint","IMPRINT",EDGE,{"disambiguationData":[TD([[subQ2,-1.0]])],"derivedFrom":subQ1}),-1.0]])]});}
            var Q9;
            {var subQ0=sQuery(id+"F0.wireOp",EDGE,"E19.MirrorCS");var subQ1=sQuery(id+"F0.wireOp",EDGE,"E6.bottom");var subQ2=makeQuery(id+"F0.imprint","INTERSECT",VERTEX,{"derivedFrom":[subQ1,subQ0]});Q9=makeQuery(id+"F0.imprint","IMPRINT",FACE,{"disambiguationData":[TD([[makeQuery(id+"F0.imprint","IMPRINT",EDGE,{"disambiguationData":[TD([[subQ2,-1.0]])],"derivedFrom":subQ1}),1.0]])]});}
            var Q10;
            {var subQ0=sQuery(id+"F0.wireOp",EDGE,"E51.MirrorCS");var subQ1=sQuery(id+"F0.wireOp",EDGE,"E19.MirrorCS");var subQ2=makeQuery(id+"F0.imprint","INTERSECT",VERTEX,{"derivedFrom":[subQ1,subQ0]});Q10=makeQuery(id+"F0.imprint","IMPRINT",FACE,{"disambiguationData":[TD([[makeQuery(id+"F0.imprint","IMPRINT",EDGE,{"disambiguationData":[TD([[subQ2,1.0]])],"derivedFrom":subQ1}),1.0]])]});}
            var Q11;
            {var subQ5=sQuery(id+"F0.wireOp",EDGE,"E19.MirrorCS");var subQ7=sQuery(id+"F0.wireOp",EDGE,"E20.MirrorCS");var subQ8=makeQuery(id+"F0.imprint","INTERSECT",VERTEX,{"derivedFrom":[subQ5,subQ7]});Q11=makeQuery(id+"F0.imprint","IMPRINT",FACE,{"disambiguationData":[TD([[makeQuery(id+"F0.imprint","IMPRINT",EDGE,{"disambiguationData":[TD([[subQ8,-1.0]])],"derivedFrom":subQ5}),1.0]])]});}
            var Q12;
            {var subQ5=sQuery(id+"F0.wireOp",EDGE,"E20.MirrorCS");var subQ8=sQuery(id+"F0.wireOp",EDGE,"E18.MirrorCS");var subQ11=makeQuery(id+"F0.imprint","INTERSECT",VERTEX,{"derivedFrom":[subQ8,subQ5]});Q12=makeQuery(id+"F0.imprint","IMPRINT",FACE,{"disambiguationData":[TD([[makeQuery(id+"F0.imprint","IMPRINT",EDGE,{"disambiguationData":[TD([[subQ11,-1.0]])],"derivedFrom":subQ8}),-1.0]])]});}
            var Q13;
            {var subQ0=sQuery(id+"F0.wireOp",EDGE,"E52.MirrorCS");var subQ1=sQuery(id+"F0.wireOp",EDGE,"E18.MirrorCS");var subQ2=makeQuery(id+"F0.imprint","INTERSECT",VERTEX,{"derivedFrom":[subQ1,subQ0]});Q13=makeQuery(id+"F0.imprint","IMPRINT",FACE,{"disambiguationData":[TD([[makeQuery(id+"F0.imprint","IMPRINT",EDGE,{"disambiguationData":[TD([[subQ2,-1.0]])],"derivedFrom":subQ1}),-1.0]])]});}
            extrude(context, id + "F5", {"entities" : qUnion([Q0, Q1, Q2, Q3, Q4, Q5, Q6, Q7, Q8, Q9, Q10, Q11, Q12, Q13]), "operationType" : NewBodyOperationType.ADD, "depth" : 10.5 * mm, "offsetDistance" : 25 * mm});
        }
        {
            var Q0;
            {var subQ0=sQuery(id+"F0.wireOp",EDGE,"E68.5");var subQ1=sQuery(id+"F0.wireOp",EDGE,"E9.MirrorCS");var subQ2=makeQuery(id+"F0.imprint","INTERSECT",VERTEX,{"derivedFrom":[subQ1,subQ0]});Q0=makeQuery(id+"F0.imprint","IMPRINT",FACE,{"disambiguationData":[TD([[makeQuery(id+"F0.imprint","IMPRINT",EDGE,{"disambiguationData":[TD([[subQ2,-1.0]])],"derivedFrom":subQ1}),1.0]])]});}
            var Q1;
            {var subQ3=sQuery(id+"F0.wireOp",EDGE,"E9.MirrorCS");var subQ9=sQuery(id+"F0.wireOp",EDGE,"E68.5");var subQ11=makeQuery(id+"F0.imprint","INTERSECT",VERTEX,{"derivedFrom":[subQ3,subQ9]});Q1=makeQuery(id+"F0.imprint","IMPRINT",FACE,{"disambiguationData":[TD([[makeQuery(id+"F0.imprint","IMPRINT",EDGE,{"disambiguationData":[TD([[subQ11,-1.0]])],"derivedFrom":subQ3}),-1.0]])]});}
            var Q2;
            {var subQ0=sQuery(id+"F0.wireOp",EDGE,"E68.4");var subQ1=sQuery(id+"F0.wireOp",EDGE,"E10.MirrorCS");var subQ2=makeQuery(id+"F0.imprint","INTERSECT",VERTEX,{"derivedFrom":[subQ1,subQ0]});Q2=makeQuery(id+"F0.imprint","IMPRINT",FACE,{"disambiguationData":[TD([[makeQuery(id+"F0.imprint","IMPRINT",EDGE,{"disambiguationData":[TD([[subQ2,-1.0]])],"derivedFrom":subQ1}),-1.0]])]});}
            var Q3;
            {var subQ0=sQuery(id+"F0.wireOp",EDGE,"E68.3");var subQ1=sQuery(id+"F0.wireOp",EDGE,"E6.top");var subQ2=makeQuery(id+"F0.imprint","INTERSECT",VERTEX,{"derivedFrom":[subQ1,subQ0]});Q3=makeQuery(id+"F0.imprint","IMPRINT",FACE,{"disambiguationData":[TD([[makeQuery(id+"F0.imprint","IMPRINT",EDGE,{"disambiguationData":[TD([[subQ2,-1.0]])],"derivedFrom":subQ1}),-1.0]])]});}
            var Q4;
            {var subQ3=sQuery(id+"F0.wireOp",EDGE,"E6.bottom");var subQ9=sQuery(id+"F0.wireOp",EDGE,"E68.1");var subQ10=makeQuery(id+"F0.imprint","INTERSECT",VERTEX,{"derivedFrom":[subQ3,subQ9]});Q4=makeQuery(id+"F0.imprint","IMPRINT",FACE,{"disambiguationData":[TD([[makeQuery(id+"F0.imprint","IMPRINT",EDGE,{"disambiguationData":[TD([[subQ10,-1.0]])],"derivedFrom":subQ3}),-1.0]])]});}
            var Q5;
            {var subQ0=sQuery(id+"F0.wireOp",EDGE,"E68.1");var subQ1=sQuery(id+"F0.wireOp",EDGE,"E6.bottom");var subQ2=makeQuery(id+"F0.imprint","INTERSECT",VERTEX,{"derivedFrom":[subQ1,subQ0]});Q5=makeQuery(id+"F0.imprint","IMPRINT",FACE,{"disambiguationData":[TD([[makeQuery(id+"F0.imprint","IMPRINT",EDGE,{"disambiguationData":[TD([[subQ2,-1.0]])],"derivedFrom":subQ1}),1.0]])]});}
            var Q6;
            {var subQ0=sQuery(id+"F0.wireOp",EDGE,"E67.5");var subQ1=sQuery(id+"F0.wireOp",EDGE,"E51.MirrorCS");var subQ2=makeQuery(id+"F0.imprint","INTERSECT",VERTEX,{"derivedFrom":[subQ1,subQ0]});Q6=makeQuery(id+"F0.imprint","IMPRINT",FACE,{"disambiguationData":[TD([[makeQuery(id+"F0.imprint","IMPRINT",EDGE,{"disambiguationData":[TD([[subQ2,-1.0]])],"derivedFrom":subQ1}),-1.0]])]});}
            var Q7;
            {var subQ1=sQuery(id+"F0.wireOp",EDGE,"E68.1");var subQ3=sQuery(id+"F0.wireOp",EDGE,"E52.MirrorCS");var subQ4=makeQuery(id+"F0.imprint","INTERSECT",VERTEX,{"derivedFrom":[subQ3,subQ1]});Q7=makeQuery(id+"F0.imprint","IMPRINT",FACE,{"disambiguationData":[TD([[makeQuery(id+"F0.imprint","IMPRINT",EDGE,{"disambiguationData":[TD([[subQ4,-1.0]])],"derivedFrom":subQ3}),1.0]])]});}
            var Q8;
            {var subQ5=sQuery(id+"F0.wireOp",EDGE,"E67.3");var subQ8=sQuery(id+"F0.wireOp",EDGE,"E52.MirrorCS");var subQ9=makeQuery(id+"F0.imprint","INTERSECT",VERTEX,{"derivedFrom":[subQ8,subQ5]});Q8=makeQuery(id+"F0.imprint","IMPRINT",FACE,{"disambiguationData":[TD([[makeQuery(id+"F0.imprint","IMPRINT",EDGE,{"disambiguationData":[TD([[subQ9,-1.0]])],"derivedFrom":subQ8}),1.0]])]});}
            var Q9;
            {var subQ0=sQuery(id+"F0.wireOp",EDGE,"E67.3");var subQ1=sQuery(id+"F0.wireOp",EDGE,"E52.MirrorCS");var subQ2=makeQuery(id+"F0.imprint","INTERSECT",VERTEX,{"derivedFrom":[subQ1,subQ0]});Q9=makeQuery(id+"F0.imprint","IMPRINT",FACE,{"disambiguationData":[TD([[makeQuery(id+"F0.imprint","IMPRINT",EDGE,{"disambiguationData":[TD([[subQ2,-1.0]])],"derivedFrom":subQ1}),-1.0]])]});}
            var Q10;
            {var subQ0=sQuery(id+"F0.wireOp",EDGE,"E68.3");var subQ9=sQuery(id+"F0.wireOp",EDGE,"E50");var subQ11=makeQuery(id+"F0.imprint","INTERSECT",VERTEX,{"derivedFrom":[subQ9,subQ0]});Q10=makeQuery(id+"F0.imprint","IMPRINT",FACE,{"disambiguationData":[TD([[makeQuery(id+"F0.imprint","IMPRINT",EDGE,{"disambiguationData":[TD([[subQ11,-1.0]])],"derivedFrom":subQ9}),-1.0]])]});}
            var Q11;
            {var subQ0=sQuery(id+"F0.wireOp",EDGE,"E67.4");var subQ1=sQuery(id+"F0.wireOp",EDGE,"E48");var subQ2=makeQuery(id+"F0.imprint","INTERSECT",VERTEX,{"derivedFrom":[subQ1,subQ0]});Q11=makeQuery(id+"F0.imprint","IMPRINT",FACE,{"disambiguationData":[TD([[makeQuery(id+"F0.imprint","IMPRINT",EDGE,{"disambiguationData":[TD([[subQ2,-1.0]])],"derivedFrom":subQ1}),1.0]])]});}
            var Q12;
            {var subQ0=sQuery(id+"F0.wireOp",EDGE,"E67.1");var subQ1=sQuery(id+"F0.wireOp",EDGE,"E49");var subQ2=makeQuery(id+"F0.imprint","INTERSECT",VERTEX,{"derivedFrom":[subQ1,subQ0]});Q12=makeQuery(id+"F0.imprint","IMPRINT",FACE,{"disambiguationData":[TD([[makeQuery(id+"F0.imprint","IMPRINT",EDGE,{"disambiguationData":[TD([[subQ2,-1.0]])],"derivedFrom":subQ1}),-1.0]])]});}
            var Q13;
            {var subQ6=sQuery(id+"F0.wireOp",EDGE,"E67.1");var subQ9=sQuery(id+"F0.wireOp",EDGE,"E50");var subQ10=makeQuery(id+"F0.imprint","INTERSECT",VERTEX,{"derivedFrom":[subQ9,subQ6]});Q13=makeQuery(id+"F0.imprint","IMPRINT",FACE,{"disambiguationData":[TD([[makeQuery(id+"F0.imprint","IMPRINT",EDGE,{"disambiguationData":[TD([[subQ10,-1.0]])],"derivedFrom":subQ9}),-1.0]])]});}
            extrude(context, id + "F6", {"entities" : qUnion([Q0, Q1, Q2, Q3, Q4, Q5, Q6, Q7, Q8, Q9, Q10, Q11, Q12, Q13]), "operationType" : NewBodyOperationType.ADD, "depth" : (10.5 + 5.5) * mm, "offsetDistance" : 25 * mm});
        }
        {
            var Q0;
            {var subQ5=sQuery(id+"F0.wireOp",EDGE,"E69.top");Q0=makeQuery(id+"F0.imprint","IMPRINT",FACE,{"disambiguationData":[TD([[makeQuery(id+"F0.imprint","IMPRINT",EDGE,{"derivedFrom":subQ5}),1.0]])]});}
            var Q1;
            {var subQ5=sQuery(id+"F0.wireOp",EDGE,"E69.bottom");Q1=makeQuery(id+"F0.imprint","IMPRINT",FACE,{"disambiguationData":[TD([[makeQuery(id+"F0.imprint","IMPRINT",EDGE,{"derivedFrom":subQ5}),-1.0]])]});}
            var Q2;
            {var subQ0=sQuery(id+"F0.wireOp",EDGE,"E74.MirrorCS");Q2=makeQuery(id+"F0.imprint","IMPRINT",FACE,{"disambiguationData":[TD([[makeQuery(id+"F0.imprint","IMPRINT",EDGE,{"derivedFrom":subQ0}),1.0]])]});}
            var Q3;
            {var subQ0=sQuery(id+"F0.wireOp",EDGE,"E72");Q3=makeQuery(id+"F0.imprint","IMPRINT",FACE,{"disambiguationData":[TD([[makeQuery(id+"F0.imprint","IMPRINT",EDGE,{"derivedFrom":subQ0}),-1.0]])]});}
            var Q4;
            {var subQ0=sQuery(id+"F0.wireOp",EDGE,"E70.MirrorCS");var subQ1=sQuery(id+"F0.wireOp",EDGE,"E20.MirrorCS");var subQ2=makeQuery(id+"F0.imprint","INTERSECT",VERTEX,{"derivedFrom":[subQ1,subQ0]});Q4=makeQuery(id+"F0.imprint","IMPRINT",FACE,{"disambiguationData":[TD([[makeQuery(id+"F0.imprint","IMPRINT",EDGE,{"disambiguationData":[TD([[subQ2,-1.0]])],"derivedFrom":subQ1}),-1.0]])]});}
            var Q5;
            {var subQ0=sQuery(id+"F0.wireOp",EDGE,"E70.MirrorCS");var subQ1=sQuery(id+"F0.wireOp",EDGE,"E67.0");var subQ2=makeQuery(id+"F0.imprint","INTERSECT",VERTEX,{"derivedFrom":[subQ1,subQ0]});Q5=makeQuery(id+"F0.imprint","IMPRINT",FACE,{"disambiguationData":[TD([[makeQuery(id+"F0.imprint","IMPRINT",EDGE,{"disambiguationData":[TD([[subQ2,-1.0]])],"derivedFrom":subQ1}),1.0]])]});}
            var Q6;
            {var subQ5=sQuery(id+"F0.wireOp",EDGE,"E74.MirrorCS");Q6=makeQuery(id+"F0.imprint","IMPRINT",FACE,{"disambiguationData":[TD([[makeQuery(id+"F0.imprint","IMPRINT",EDGE,{"derivedFrom":subQ5}),-1.0]])]});}
            var Q7;
            {var subQ7=sQuery(id+"F0.wireOp",EDGE,"E75.MirrorCS");Q7=makeQuery(id+"F0.imprint","IMPRINT",FACE,{"disambiguationData":[TD([[makeQuery(id+"F0.imprint","IMPRINT",EDGE,{"derivedFrom":subQ7}),1.0]])]});}
            var Q8;
            {var subQ0=sQuery(id+"F0.wireOp",EDGE,"E72");Q8=makeQuery(id+"F0.imprint","IMPRINT",FACE,{"disambiguationData":[TD([[makeQuery(id+"F0.imprint","IMPRINT",EDGE,{"derivedFrom":subQ0}),1.0]])]});}
            var Q9;
            {var subQ5=sQuery(id+"F0.wireOp",EDGE,"E73");Q9=makeQuery(id+"F0.imprint","IMPRINT",FACE,{"disambiguationData":[TD([[makeQuery(id+"F0.imprint","IMPRINT",EDGE,{"derivedFrom":subQ5}),-1.0]])]});}
            extrude(context, id + "F7", {"entities" : qUnion([Q0, Q1, Q2, Q3, Q4, Q5, Q6, Q7, Q8, Q9]), "operationType" : NewBodyOperationType.ADD, "depth" : (10.5 - 5 / 2) * mm, "offsetDistance" : 25 * mm});
        }
        {
            var Q0;
            Q0=makeQuery(id+"F0.imprint","IMPRINT",FACE,{"disambiguationData":[TD([[makeQuery(id+"F0.imprint","IMPRINT",EDGE,{"derivedFrom":sQuery(id+"F0.wireOp",EDGE,"E58")}),-1.0]])]});
            var Q1;
            Q1=makeQuery(id+"F0.imprint","IMPRINT",FACE,{"disambiguationData":[TD([[makeQuery(id+"F0.imprint","IMPRINT",EDGE,{"derivedFrom":sQuery(id+"F0.wireOp",EDGE,"E59.MirrorC")}),1.0]])]});
            extrude(context, id + "F8", {"entities" : qUnion([Q0, Q1]), "operationType" : NewBodyOperationType.ADD, "depth" : 12.5 * mm, "offsetDistance" : 25 * mm});
        }
        {
            var Q0;
            Q0=makeQuery(id+"F0.imprint","IMPRINT",FACE,{"disambiguationData":[TD([[makeQuery(id+"F0.imprint","IMPRINT",EDGE,{"derivedFrom":sQuery(id+"F0.wireOp",EDGE,"E59.MirrorC")}),-1.0]])]});
            var Q1;
            Q1=makeQuery(id+"F0.imprint","IMPRINT",FACE,{"disambiguationData":[TD([[makeQuery(id+"F0.imprint","IMPRINT",EDGE,{"derivedFrom":sQuery(id+"F0.wireOp",EDGE,"E58")}),1.0]])]});
            extrude(context, id + "F9", {"entities" : qUnion([Q0, Q1]), "operationType" : NewBodyOperationType.ADD, "depth" : (15 - 9 - 2.5) * mm, "offsetDistance" : 25 * mm});
        }
        {
            var Q0;
            Q0=makeQuery(id+"F5.opExtrude","CAP_EDGE",EDGE,{"disambiguationData":[OSD([sQuery(id+"F0.wireOp",EDGE,"E17.MirrorCS")])],"isStart":true});
            var Q1;
            Q1=makeQuery(id+"F5.opExtrude","CAP_EDGE",EDGE,{"disambiguationData":[OSD([sQuery(id+"F0.wireOp",EDGE,"E19.MirrorCS")])],"isStart":true});
            var Q2;
            {var subQ0=sQuery(id+"F0.wireOp",EDGE,"E69.top");var subQ1=sQuery(id+"F0.wireOp",EDGE,"E15");Q2=makeQuery(id+"F7.boolean.opBoolean","MERGE",EDGE,{"derivedFrom":[makeQuery(id+"F5.opExtrude","CAP_EDGE",EDGE,{"disambiguationData":[OSD([subQ1]),TDD([makeQuery(id+"F0.imprint","IMPRINT",EDGE,{"disambiguationData":[TD([[makeQuery(id+"F0.imprint","INTERSECT",VERTEX,{"derivedFrom":[subQ1,sQuery(id+"F0.wireOp",EDGE,"E17.MirrorCS")]}),-1.0]])],"derivedFrom":subQ1})])],"isStart":true}),makeQuery(id+"F5.opExtrude","CAP_EDGE",EDGE,{"disambiguationData":[OSD([subQ1]),TDD([makeQuery(id+"F0.imprint","IMPRINT",EDGE,{"disambiguationData":[TD([[makeQuery(id+"F0.imprint","INTERSECT",VERTEX,{"derivedFrom":[subQ1,sQuery(id+"F0.wireOp",EDGE,"E16")]}),1.0]])],"derivedFrom":subQ1})])],"isStart":true}),makeQuery(id+"F7.opExtrude","CAP_EDGE",EDGE,{"disambiguationData":[OSD([subQ0])],"isStart":true})]});}
            var Q3;
            {var subQ0=sQuery(id+"F0.wireOp",EDGE,"E20.MirrorCS");Q3=makeQuery(id+"F7.boolean.opBoolean","MERGE",EDGE,{"derivedFrom":[makeQuery(id+"F5.opExtrude","CAP_EDGE",EDGE,{"disambiguationData":[OSD([subQ0]),TDD([makeQuery(id+"F0.imprint","IMPRINT",EDGE,{"disambiguationData":[TD([[makeQuery(id+"F0.imprint","INTERSECT",VERTEX,{"derivedFrom":[sQuery(id+"F0.wireOp",EDGE,"E19.MirrorCS"),subQ0]}),-1.0]])],"derivedFrom":subQ0})])],"isStart":true}),makeQuery(id+"F5.opExtrude","CAP_EDGE",EDGE,{"disambiguationData":[OSD([subQ0]),TDD([makeQuery(id+"F0.imprint","IMPRINT",EDGE,{"disambiguationData":[TD([[makeQuery(id+"F0.imprint","INTERSECT",VERTEX,{"derivedFrom":[sQuery(id+"F0.wireOp",EDGE,"E18.MirrorCS"),subQ0]}),1.0]])],"derivedFrom":subQ0})])],"isStart":true}),makeQuery(id+"F7.opExtrude","CAP_EDGE",EDGE,{"disambiguationData":[OSD([subQ0])],"isStart":true})]});}
            var Q4;
            Q4=makeQuery(id+"F5.opExtrude","CAP_EDGE",EDGE,{"disambiguationData":[OSD([sQuery(id+"F0.wireOp",EDGE,"E18.MirrorCS")])],"isStart":true});
            var Q5;
            Q5=makeQuery(id+"F5.opExtrude","CAP_EDGE",EDGE,{"disambiguationData":[OSD([sQuery(id+"F0.wireOp",EDGE,"E16")])],"isStart":true});
            fillet(context, id + "F10", {"entities" : qUnion([Q0, Q1, Q2, Q3, Q4, Q5]), "radius" : 3 * mm, "tangentPropagation" : true, "allowEdgeOverflow" : false});
        }
    });
